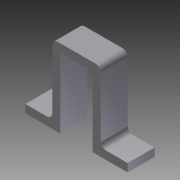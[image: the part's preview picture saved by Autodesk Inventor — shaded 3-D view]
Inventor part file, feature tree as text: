
AUTODESK INVENTOR PART (.ipt)
format: ipt  version: 2012 (Build 160160000, 160)  size: 95,232 bytes
history: native  units: mm
features: extrude x1, sketch x1
ambient origin geometry x8: Origin, YZ Plane, XZ Plane, XY Plane, X Axis, Y Axis, Z Axis, Center Point
bodies: Solid1 (feature_tree)
feature tree (2):
  extrude  "Extrusion1"  Depth=26.0mm
  sketch  "Sketch1"  dims[d2=12.0mm d3=26.0mm d4=13.0mm d5=13.0mm d6=3.0mm d7=26.0mm d8=10.0mm d9=0.0mm d10=2.0mm d11=10.0mm]
